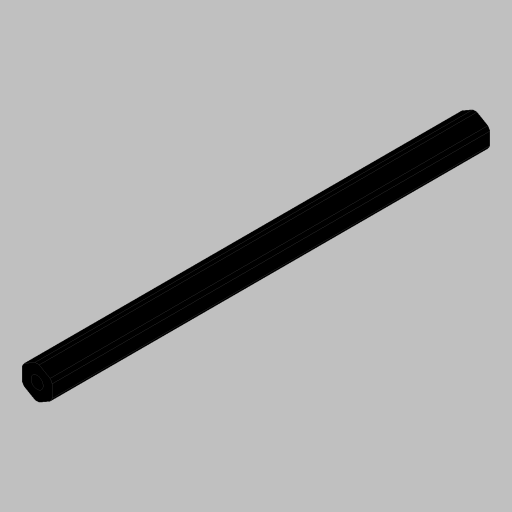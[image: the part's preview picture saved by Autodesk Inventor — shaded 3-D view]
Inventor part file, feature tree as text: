
AUTODESK INVENTOR PART (.ipt)
format: ipt  version: 2023.4 (Build 274418000, 418)  size: 119,808 bytes
history: native  units: in
note: dims shown in document units (in); Inventor stores cm internally (conversion verified against a paired STEP export)
features: extrude x2, projected_geometry x2, hole x1
ambient origin geometry x8: Origin, YZ Plane, XZ Plane, XY Plane, X Axis, Y Axis, Z Axis, Center Point
bodies: Solid1 (feature_tree)
feature tree (5):
  extrude  "Extrusion1"  TaperAngle=0.0deg  [1 undecoded]
  hole  "Hole1"  [1 undecoded]
  extrude  "Extrusion3"  TaperAngle=0.0deg  [1 undecoded]
  projected_geometry  "Project Cut Edges1"
  projected_geometry  "Project Cut Edges2"
note: 3 required parameter values undecoded (feature->parameter linkage not recoverable at this tier; creation-order binding heuristic only, values carry confidence <= 0.55)
